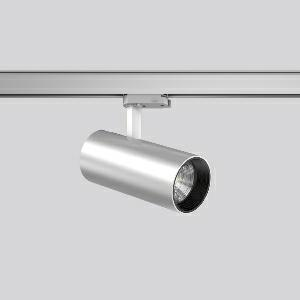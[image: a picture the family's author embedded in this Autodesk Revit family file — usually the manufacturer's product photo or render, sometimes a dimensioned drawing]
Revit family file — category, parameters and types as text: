
# Revit family: deecos_s_mini_742208_004_2_76_eb1c
name_source: partatom
category: Lighting Fixtures
units: mm (PartAtom-declared; Revit-internal decimal feet)

## family parameters
Cut with Voids When Loaded = No
Host = Face
Light Source = No
Part Type = Normal
Room Calculation Point = No
Round Connector Dimension = Use Diameter
Shared = No

## types (1)
- DEECOS S mini (1 x LED Modul 927, 2700 lm, 2700)
    Apparent Load = 29 VA
    Approval mark = CE
    CIE Flux Codes = 98 100 100 100 100
    Color Rendering = 92
    Color Temperature = 2700
    Default Elevation = 1800 mm
    Description = Series: DEECOS S mini
LED surface-mounted projector in modern design with no visible cooling ribs. Housing: die-cast aluminium, powder-coated. Rotation range: 356°. Swivel range: 90°. Black plastic ring and recessed LED to prevent glare from the side. Optical assembly with lens made of plastic (polycarbonate) for the best homogeneous light distribution - can be changed without tools. Best colour rendering index Ra>90. With adapter for RZB 3-circuit DALI tracks. Suitable for Track on ceiling, Wall track. High quality converter without flickering and stroboscopic effect. The following accessories can be mounted without use of tools: interchangeable lenses, decorative glasses, honeycomb louvre, clear and frosted diffusers, white interchangeable plastic ring. 
Colour: silver
Diameter: 87 mm
Height: 214 mm
Lamp: LED
Socket: without socket
Colour temperature: 2700K
Colour rendering index (CRI): 92
System power: 29 W
Rated luminous flux: 2700 lm
Luminous efficiency: 93 lm/W
Control gear: Converter, dimmable, DALI
Protection class: I
Type of protection: IP 20
    Height = 214 mm
    Lamp = 1 x LED Modul 927
    Lamp Light Flux = 2700 lm
    Lamp count = 1
    Length = 87 mm
    Lifetime = 50000 h
    Luminous efficacy = 93 lm/W
    Manufacturer = RZB
    ModVariant = No
    Model = 742208.004.2.76
    Mounting Place = Ceiling
    Mounting Type = Rail mounted
    Number of Poles = 1
    OnlyDefault = Yes
    Power Factor = 1
    Product Name = DEECOS S mini
    Product group = Track mounted projectors
    ProductGroupID = 301
    Protection Class = Protection class I
    Protection Degree = IP 20
    RLX_Detail_Level = 1
    RLX_Emergency_Light_Flux = 0 lm
    RLX_Emergency_Type = 0
    RLX_Emergency_Type_DB = No
    RlxData = <blob elided: 37401 chars, md5=4d12bb12>
    Socket = socket
    Standby Power = 0 W
    System Light Flux = 2700 lm
    System Power = 29 W
    Type Comments = Product without accessories
    Type Image = 741930.004.jpg
    URL = http://relux.com
    VarID = ---
    Voltage = 230 V
    Voltage Range = 220-240 V
    Weight = 0.00 kg
    Width = 0 mm  [stored 0 ft]

note: [stored X ft] marks values corroborated as IEEE doubles in the binary element streams (Revit-internal decimal feet)

## geometry (parser evidence)
native form markers: Blend x4, Sweep x11
no freeform markers — native parametric forms only
